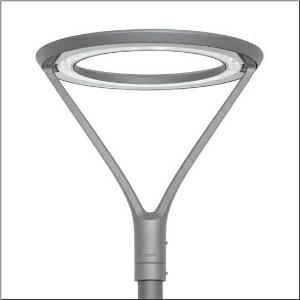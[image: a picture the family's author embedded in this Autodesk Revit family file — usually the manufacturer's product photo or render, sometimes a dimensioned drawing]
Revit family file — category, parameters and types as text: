
# Revit family: dl_r__20___pl1_2s_5xa51283ns008_3424
name_source: partatom
category: Lighting Fixtures
units: mm (PartAtom-declared; Revit-internal decimal feet)

## family parameters
Cut with Voids When Loaded = No
Host = Face
Light Source = No
Part Type = Normal
Room Calculation Point = No
Round Connector Dimension = Use Diameter
Shared = No

## types (1)
- --- (1 x LED, 3060 lm, 23.2 W, 4000K)
    Apparent Load = 23 VA
    CIE Flux Codes = 33 78 99 100 100
    Color Rendering = 70
    Color Temperature = 4000K
    Default Elevation = 1800 mm
    Description = DL® 20, mast luminaire, primary light control with reflector, highly specular, primary optical cover: cover, of toughened safety glass of clear glass with excellent transmission level, light distribution: PL1.2s, light emission: direct distribution, primary light characteristic: symmetric, installation type: post-top, LED, High Power LED, rated luminous flux: 3.030lm, luminous efficacy: 111lm/W, light colour: 740, colour temperature: 4000K, control gear: Plus, control: overheat protection, power reduction, digital communication interface, constant luminous flux control, time-dependent luminous flux control, flexible luminous flux parameterisation, electronic power reduction, mains connection: 230..240V, 50/60Hz, connection cable pre-assembled, cable length: 5m, start of lifetime: 27W, end of service life: 28W, reduction: 14W, luminaire housing, upper part, of cast aluminium, powder-coated, Siteco® metallic grey (DB 702S), diameter: 690mm, height: 690mm, spigot size: 76mm (post-top), mounting height: 4..6m, luminaire housing, of cast aluminium, powder-coated, Siteco® metallic grey (DB 702S), equipment: standard, protection rating (complete): IP66, insulation class (complete): insulation class II (safety insulation), certification: CE, ENEC, VDE, impact resistance: IK08, permissible operating ambient temperature: -25..+35°C, standard-compliant lighting for roads and squares, packaging unit: 1 piece

Light Distribution: PL1.2s
    Height = 690 mm
    Lamp = 1 x LED
    Lamp Light Flux = 3060 lm
    Lamp Power = 23.2 W
    Lamp count = 1
    Length = 690 mm
    Luminous efficacy = 132 lm/W
    Manufacturer = Siteco
    ModVariant = No
    Model = 5XA51283NS008
    Number of Poles = 1
    OnlyDefault = Yes
    Power Factor = 1
    Product Name = DL® 20 | PL1.2s
    Product group = mast luminaire | pylon top
    ProductGroupID = 6100
    Protection Class = Protection class II
    Protection Degree = IP 66
    RLX_Detail_Level = 1
    RLX_Emergency_Light_Flux = 0 lm
    RLX_Emergency_Type = 0
    RLX_Emergency_Type_DB = No
    RlxData = <blob elided: 203893 chars, md5=a33fe6b9>
    Socket = socket
    Standby Power = 0 W
    System Light Flux = 3060 lm
    System Power = 23 W
    Type Comments = factory setting: luminous flux: 100 % | dim-lin: 254 | 310 mA
    Type Image = l_1006001.jpg
    URL = http://relux.com
    VarID = @adj_076642
    Voltage = 0 V
    Weight = 0.00 kg
    Width = 0 mm  [stored 0 ft]

note: [stored X ft] marks values corroborated as IEEE doubles in the binary element streams (Revit-internal decimal feet)

## geometry (parser evidence)
native form markers: Blend x4, Sweep x10
no freeform markers — native parametric forms only
